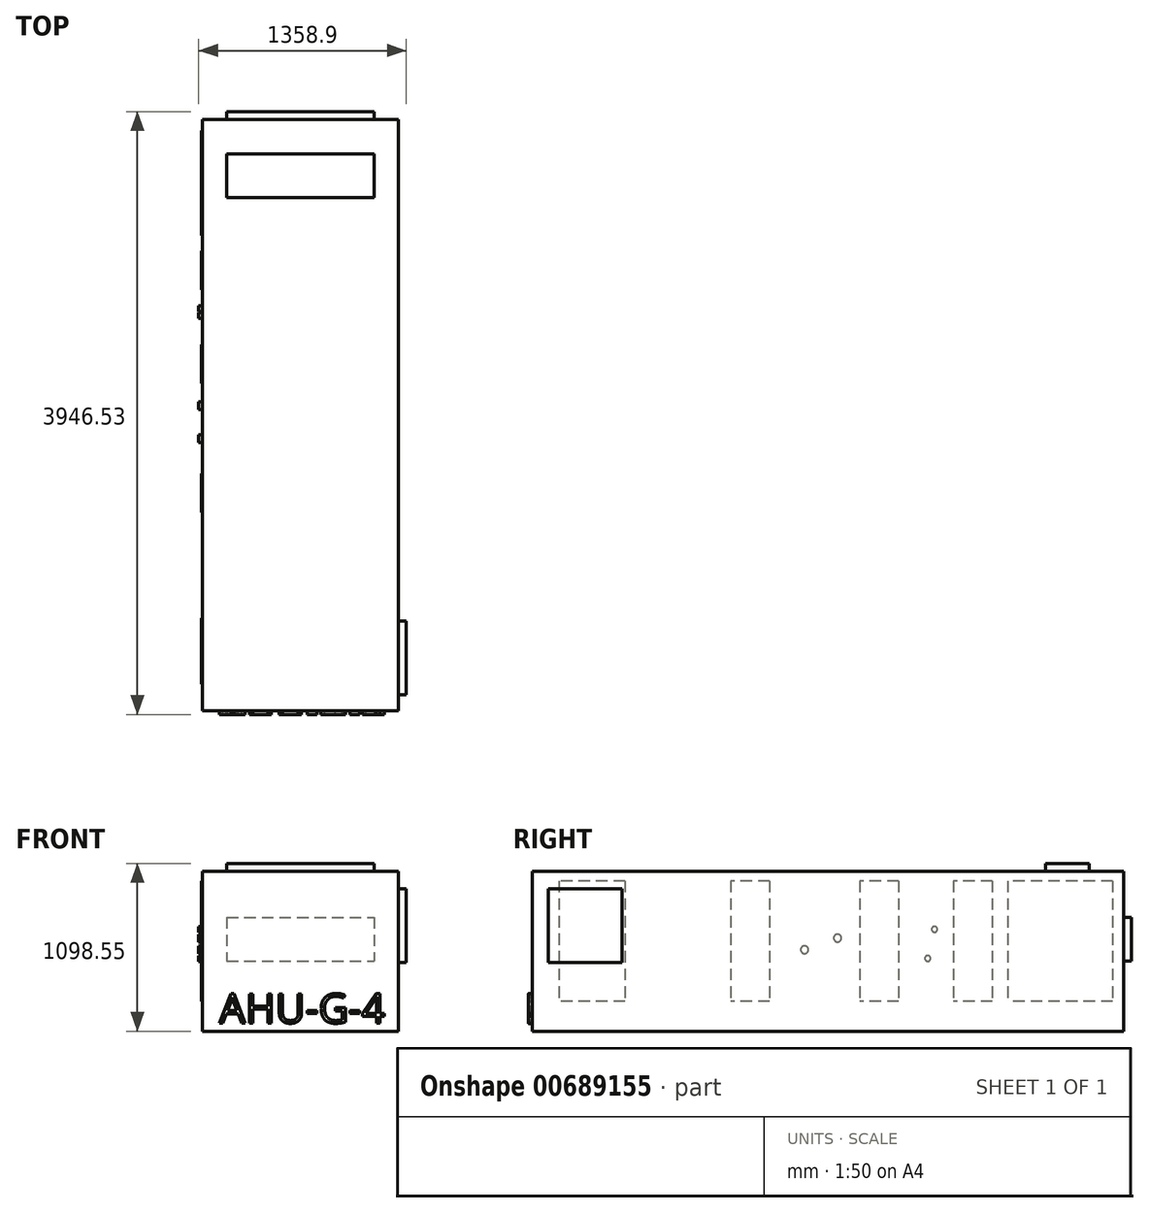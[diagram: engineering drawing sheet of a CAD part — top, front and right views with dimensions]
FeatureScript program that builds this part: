
annotation { "Feature Type Name" : "Feature", "Feature Type Description" : "" }
export const myFeature = defineFeature(function(context is Context, id is Id, definition is map)
    precondition{}
    {
        {
            var Q0;
            Q0=qCreatedBy(makeId("Front.planeOp"),FACE);
            var sketch = newSketch(context, id + "F0", { "sketchPlane" : qUnion([Q0])});
            skLineSegment(sketch, "E0.bottom", {"start": v(-639.94, 495.31) * mm, "end": v(642.76, 495.31) * mm});
            skLineSegment(sketch, "E0.top", {"start": v(-639.94, -552.44) * mm, "end": v(642.76, -552.44) * mm});
            skLineSegment(sketch, "E0.left", {"start": v(-639.94, 495.31) * mm, "end": v(-639.94, -552.44) * mm});
            skLineSegment(sketch, "E0.right", {"start": v(642.76, 495.31) * mm, "end": v(642.76, -552.44) * mm});
            skSolve(sketch);
        }
        {
            var Q0;
            Q0=qSketchRegion(id+"F0",true);
            extrude(context, id + "F1", {"entities" : qUnion([Q0]), "depth" : 3870.32 * mm, "offsetDistance" : 25.4 * mm});
        }
        {
            var Q0;
            Q0=makeQuery(id+"F1.opExtrude","SWEPT_FACE",FACE,{"disambiguationData":[OSD([sQuery(id+"F0.wireOp",EDGE,"E0.right")])]});
            var sketch = newSketch(context, id + "F2", { "sketchPlane" : qUnion([Q0])});
            skLineSegment(sketch, "E1.bottom", {"start": v(-3765.55, 381.01) * mm, "end": v(-3282.95, 381.01) * mm});
            skLineSegment(sketch, "E1.top", {"start": v(-3765.55, -101.59) * mm, "end": v(-3282.95, -101.59) * mm});
            skLineSegment(sketch, "E1.left", {"start": v(-3765.55, 381.01) * mm, "end": v(-3765.55, -101.59) * mm});
            skLineSegment(sketch, "E1.right", {"start": v(-3282.95, 381.01) * mm, "end": v(-3282.95, -101.59) * mm});
            skSolve(sketch);
        }
        {
            var Q0;
            Q0=qSketchRegion(id+"F2",true);
            extrude(context, id + "F3", {"entities" : qUnion([Q0]), "operationType" : NewBodyOperationType.ADD, "depth" : 50.8 * mm, "offsetDistance" : 25.4 * mm});
        }
        {
            var Q0;
            Q0=makeQuery(id+"F1.opExtrude","CAP_FACE",FACE,{"disambiguationData":[OSD([sQuery(id+"F0.wireOp",EDGE,"E0.bottom"),sQuery(id+"F0.wireOp",EDGE,"E0.top"),sQuery(id+"F0.wireOp",EDGE,"E0.left"),sQuery(id+"F0.wireOp",EDGE,"E0.right")])],"isStart":false});
            var sketch = newSketch(context, id + "F4", { "sketchPlane" : qUnion([Q0])});
            skText(sketch, "E2", { "text": "AHU-G-4", "fontName": "OpenSans-Regular.ttf"});
            const initialGuessF4  = {"E2": [-0.52978, -0.49919, 1, 0, 0.19308]};
            skSetInitialGuess(sketch, initialGuessF4);
            skSolve(sketch);
        }
        {
            var Q0;
            Q0=qSketchRegion(id+"F4",true);
            extrude(context, id + "F5", {"entities" : qUnion([Q0]), "operationType" : NewBodyOperationType.ADD, "depth" : 25.4 * mm, "offsetDistance" : 25.4 * mm});
        }
        {
            var Q0;
            Q0=makeQuery(id+"F1.opExtrude","SWEPT_FACE",FACE,{"disambiguationData":[OSD([sQuery(id+"F0.wireOp",EDGE,"E0.bottom")])]});
            var sketch = newSketch(context, id + "F6", { "sketchPlane" : qUnion([Q0])});
            skLineSegment(sketch, "E3.bottom", {"start": v(-481.2, -511.17) * mm, "end": v(484, -511.17) * mm});
            skLineSegment(sketch, "E3.top", {"start": v(-481.2, -225.43) * mm, "end": v(484, -225.42) * mm});
            skLineSegment(sketch, "E3.left", {"start": v(-481.2, -511.17) * mm, "end": v(-481.2, -225.42) * mm});
            skLineSegment(sketch, "E3.right", {"start": v(484, -511.17) * mm, "end": v(484, -225.42) * mm});
            skSolve(sketch);
        }
        {
            var Q0;
            Q0=qSketchRegion(id+"F6",true);
            extrude(context, id + "F7", {"entities" : qUnion([Q0]), "operationType" : NewBodyOperationType.ADD, "depth" : 50.8 * mm, "offsetDistance" : 25.4 * mm});
        }
        {
            var Q0;
            Q0=makeQuery(id+"F1.opExtrude","CAP_FACE",FACE,{"disambiguationData":[OSD([sQuery(id+"F0.wireOp",EDGE,"E0.bottom"),sQuery(id+"F0.wireOp",EDGE,"E0.top"),sQuery(id+"F0.wireOp",EDGE,"E0.left"),sQuery(id+"F0.wireOp",EDGE,"E0.right")])],"isStart":true});
            var sketch = newSketch(context, id + "F8", { "sketchPlane" : qUnion([Q0])});
            skLineSegment(sketch, "E4.bottom", {"start": v(481.2, 193.69) * mm, "end": v(-484, 193.69) * mm});
            skLineSegment(sketch, "E4.top", {"start": v(481.2, -92.06) * mm, "end": v(-484, -92.06) * mm});
            skLineSegment(sketch, "E4.left", {"start": v(481.2, 193.69) * mm, "end": v(481.2, -92.06) * mm});
            skLineSegment(sketch, "E4.right", {"start": v(-484, 193.69) * mm, "end": v(-484, -92.06) * mm});
            skSolve(sketch);
        }
        {
            var Q0;
            Q0=qSketchRegion(id+"F8",true);
            extrude(context, id + "F9", {"entities" : qUnion([Q0]), "operationType" : NewBodyOperationType.ADD, "depth" : 50.8 * mm, "offsetDistance" : 25.4 * mm});
        }
        {
            var Q0;
            Q0=makeQuery(id+"F1.opExtrude","SWEPT_FACE",FACE,{"disambiguationData":[OSD([sQuery(id+"F0.wireOp",EDGE,"E0.left")])]});
            var sketch = newSketch(context, id + "F10", { "sketchPlane" : qUnion([Q0])});
            skLineSegment(sketch, "E5.bottom", {"start": v(73.02, 431.81) * mm, "end": v(758.83, 431.81) * mm});
            skLineSegment(sketch, "E5.top", {"start": v(73.03, -355.59) * mm, "end": v(758.83, -355.59) * mm});
            skLineSegment(sketch, "E5.left", {"start": v(73.03, 431.81) * mm, "end": v(73.03, -355.59) * mm});
            skLineSegment(sketch, "E5.right", {"start": v(758.83, 431.81) * mm, "end": v(758.83, -355.59) * mm});
            skLineSegment(sketch, "E6.bottom", {"start": v(860.43, 431.81) * mm, "end": v(1114.43, 431.81) * mm});
            skLineSegment(sketch, "E6.top", {"start": v(860.43, -355.59) * mm, "end": v(1114.43, -355.59) * mm});
            skLineSegment(sketch, "E6.left", {"start": v(860.43, 431.81) * mm, "end": v(860.43, -355.59) * mm});
            skLineSegment(sketch, "E6.right", {"start": v(1114.43, 431.81) * mm, "end": v(1114.43, -355.59) * mm});
            skLineSegment(sketch, "E7.bottom", {"start": v(1473.2, 431.81) * mm, "end": v(1727.2, 431.81) * mm});
            skLineSegment(sketch, "E7.top", {"start": v(1473.2, -355.59) * mm, "end": v(1727.2, -355.59) * mm});
            skLineSegment(sketch, "E7.left", {"start": v(1473.2, 431.81) * mm, "end": v(1473.2, -355.59) * mm});
            skLineSegment(sketch, "E7.right", {"start": v(1727.2, 431.81) * mm, "end": v(1727.2, -355.59) * mm});
            skLineSegment(sketch, "E8.bottom", {"start": v(2317.75, 431.81) * mm, "end": v(2571.75, 431.81) * mm});
            skLineSegment(sketch, "E8.top", {"start": v(2317.75, -355.59) * mm, "end": v(2571.75, -355.59) * mm});
            skLineSegment(sketch, "E8.left", {"start": v(2317.75, 431.81) * mm, "end": v(2317.75, -355.59) * mm});
            skLineSegment(sketch, "E8.right", {"start": v(2571.75, 431.81) * mm, "end": v(2571.75, -355.59) * mm});
            skLineSegment(sketch, "E9.bottom", {"start": v(3263.9, 431.81) * mm, "end": v(3695.7, 431.81) * mm});
            skLineSegment(sketch, "E9.top", {"start": v(3263.9, -355.59) * mm, "end": v(3695.7, -355.59) * mm});
            skLineSegment(sketch, "E9.left", {"start": v(3263.9, 431.81) * mm, "end": v(3263.9, -355.59) * mm});
            skLineSegment(sketch, "E9.right", {"start": v(3695.7, 431.81) * mm, "end": v(3695.7, -355.59) * mm});
            skSolve(sketch);
        }
        {
            var Q0;
            Q0 = qSketchRegion(id + "F10", true);
            extrude(context, id + "F11", {"entities" : qUnion([Q0]), "operationType" : NewBodyOperationType.ADD, "depth" : 6.35 * mm, "offsetDistance" : 25.4 * mm});
        }
        {
            var Q0;
            Q0=makeQuery(id+"F1.opExtrude","SWEPT_FACE",FACE,{"disambiguationData":[OSD([sQuery(id+"F0.wireOp",EDGE,"E0.left")])]});
            var sketch = newSketch(context, id + "F12", { "sketchPlane" : qUnion([Q0])});
            skCircle(sketch, "E10", {"center": v(1238.25, 114.31) * mm, "radius": 19.05 * mm});
            skCircle(sketch, "E11", {"center": v(1282.7, -76.19) * mm, "radius": 19.05 * mm});
            skCircle(sketch, "E12", {"center": v(1873.25, 57.16) * mm, "radius": 25.4 * mm});
            skCircle(sketch, "E13", {"center": v(2089.15, -19.04) * mm, "radius": 25.4 * mm});
            skSolve(sketch);
        }
        {
            var Q0;
            Q0 = qSketchRegion(id + "F12", true);
            extrude(context, id + "F13", {"entities" : qUnion([Q0]), "operationType" : NewBodyOperationType.ADD, "depth" : 25.4 * mm, "offsetDistance" : 25.4 * mm});
        }
    });
